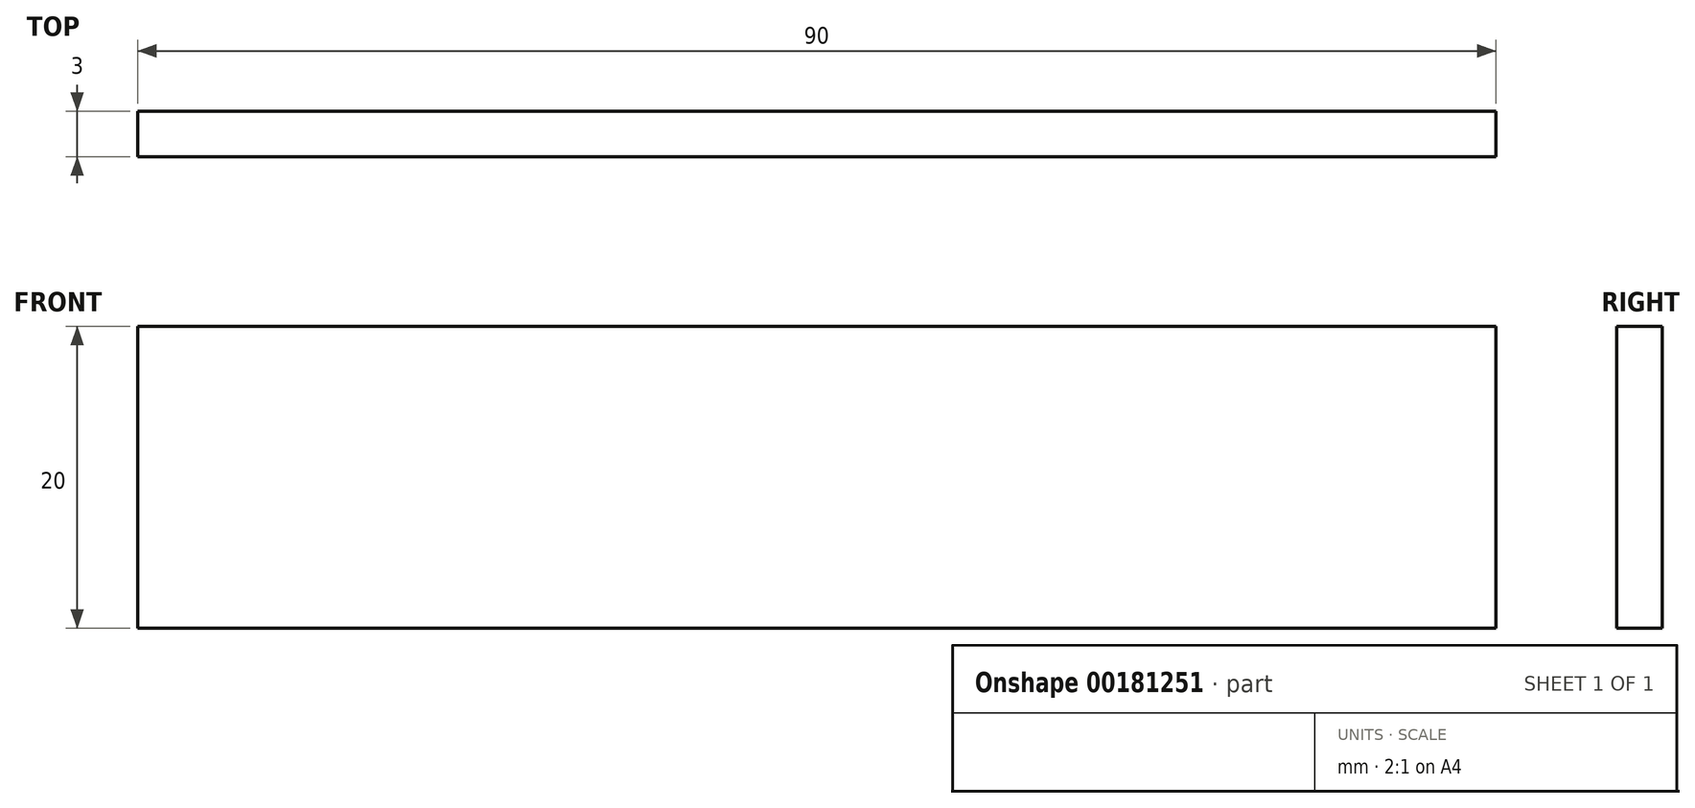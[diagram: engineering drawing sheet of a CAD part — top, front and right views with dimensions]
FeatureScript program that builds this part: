
annotation { "Feature Type Name" : "Feature", "Feature Type Description" : "" }
export const myFeature = defineFeature(function(context is Context, id is Id, definition is map)
    precondition{}
    {
        {
            var Q0;
            Q0=qCreatedBy(makeId("Front.planeOp"),FACE);
            var sketch = newSketch(context, id + "F0", { "sketchPlane" : qUnion([Q0])});
            skLineSegment(sketch, "E0.bottom", {"start": v(45, 10) * mm, "end": v(-45, 10) * mm});
            skLineSegment(sketch, "E0.top", {"start": v(45, -10) * mm, "end": v(-45, -10) * mm});
            skLineSegment(sketch, "E0.left", {"start": v(45, 10) * mm, "end": v(45, -10) * mm});
            skLineSegment(sketch, "E0.right", {"start": v(-45, 10) * mm, "end": v(-45, -10) * mm});
            skPoint(sketch, "E0.middle", {"position": v(0, 0) * mm});
            skSolve(sketch);
        }
        {
            var Q0;
            Q0=makeQuery(id+"F0.imprint","IMPRINT",FACE,{"disambiguationData":[TD([[makeQuery(id+"F0.imprint","IMPRINT",EDGE,{"derivedFrom":sQuery(id+"F0.wireOp",EDGE,"E0.bottom")}),1.0]])]});
            extrude(context, id + "F1", {"entities" : qUnion([Q0]), "depth" : 3 * mm});
        }
    });
